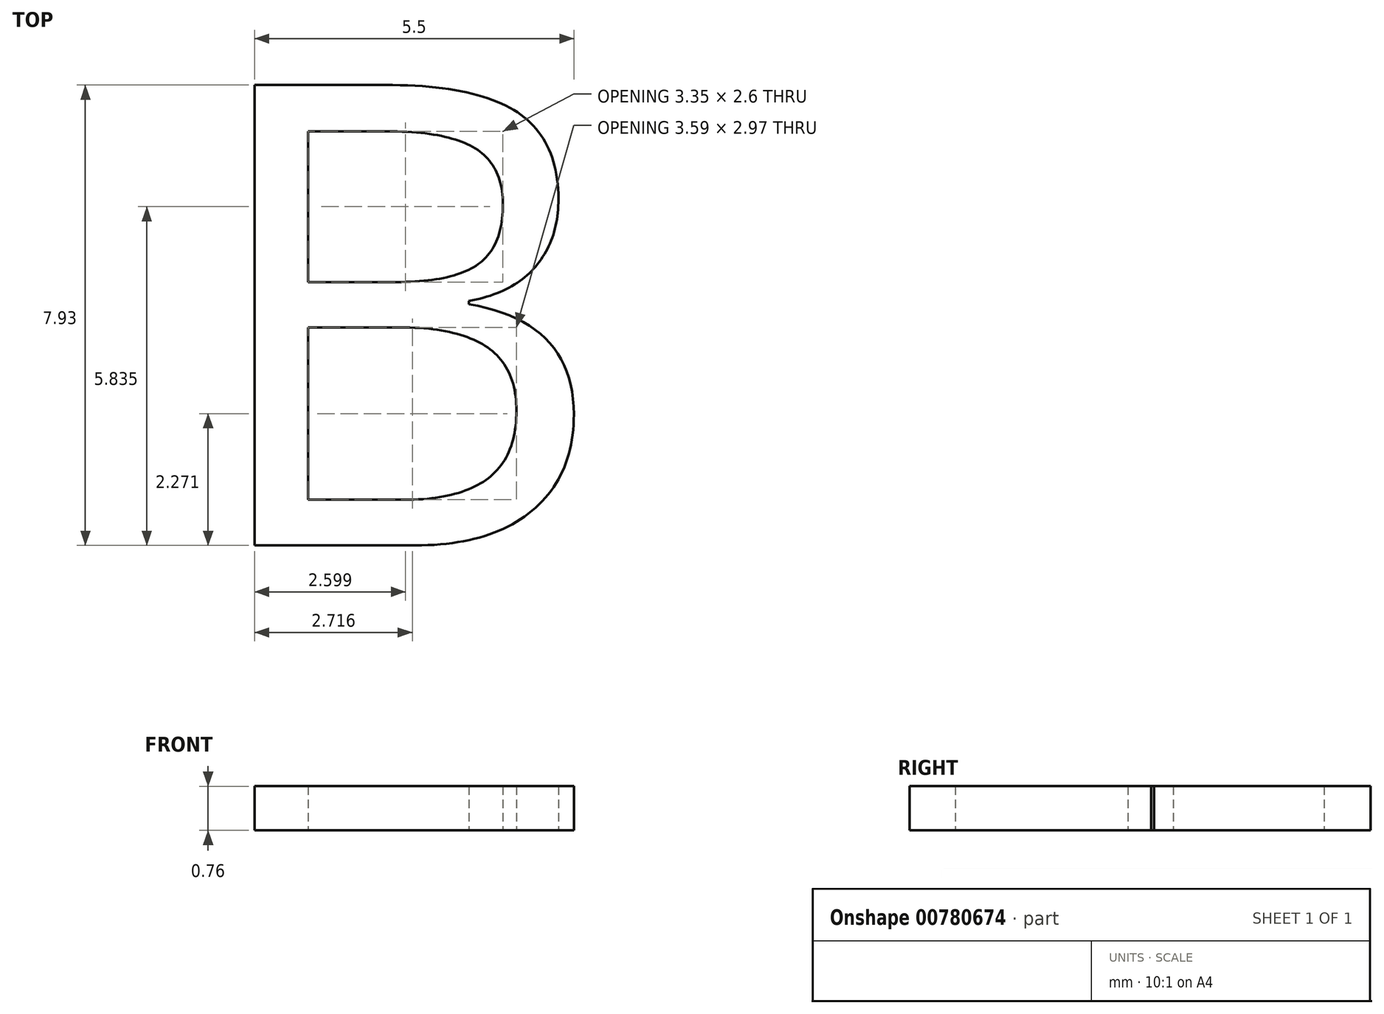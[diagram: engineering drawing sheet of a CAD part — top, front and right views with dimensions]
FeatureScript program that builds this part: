
annotation { "Feature Type Name" : "Feature", "Feature Type Description" : "" }
export const myFeature = defineFeature(function(context is Context, id is Id, definition is map)
    precondition{}
    {
        {
            var Q0;
            Q0=qCreatedBy(makeId("Top.planeOp"),FACE);
            var sketch = newSketch(context, id + "F0", { "sketchPlane" : qUnion([Q0])});
            skText(sketch, "E0", { "text": "B\n", "fontName": "OpenSans-Regular.ttf"});
            const initialGuessF0  = {"E0": [-0.0073, 0, 1, 0, 0.008]};
            skSetInitialGuess(sketch, initialGuessF0);
            skSolve(sketch);
        }
        {
            var Q0;
            Q0 = qSketchRegion(id + "F0", true);
            extrude(context, id + "F1", {"entities" : qUnion([Q0]), "depth" : 0.76 * mm, "offsetDistance" : 25.4 * mm});
        }
    });
